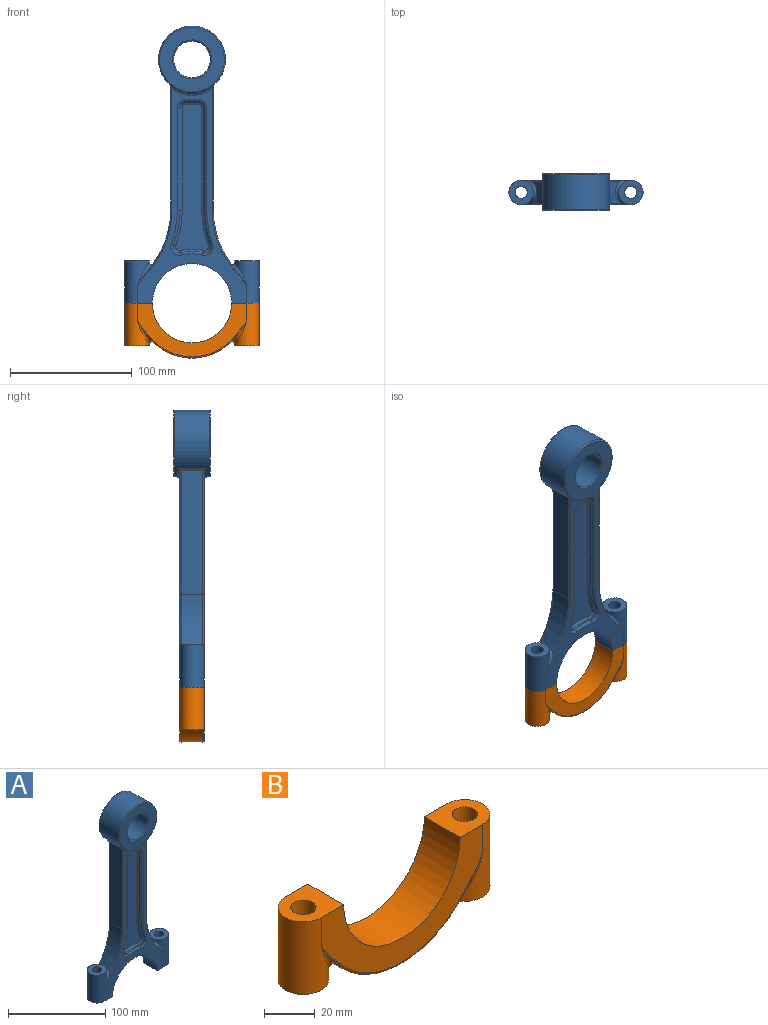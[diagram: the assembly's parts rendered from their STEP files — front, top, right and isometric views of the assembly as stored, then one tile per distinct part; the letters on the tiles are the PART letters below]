
ASSEMBLY  parts=2 mates=1
PART A: 119 faces, bbox 110.6x30.6x230.3 mm
  f0: plane 22.5x20mm, normal (0,0,-1), area 328.5mm2, adj f2,f9,f24,f29,f71
  f1: cylinder r=45mm len=0.99mm, axis (0,1,0), area 0.5mm2, adj f4,f50,f65
  f2: cylinder r=32.5mm len=65mm, axis (0,1,0), area 2042mm2, adj f0,f3,f9,f71
  f3: plane 22.5x20mm, normal (0,0,-1), area 328.5mm2, adj f2,f9,f26,f27,f71
  f4: cylinder r=75mm len=47.78mm, axis (0,1,0), area 891.8mm2, adj f1,f5,f50,f64,f69,f114
  f5: plane 101.42x19.35mm, normal (1,0,0), area 1826.5mm2, adj f4,f54,f62,f63,f112,f113
  f6: plane 101.42x19.35mm, normal (-1,0,0), area 1826.5mm2, adj f7,f52,f56,f57,f106,f107
  f7: cylinder r=75mm len=47.78mm, axis (0,1,0), area 891.8mm2, adj f6,f8,f51,f58,f70,f108
  f8: cylinder r=45mm len=0.99mm, axis (0,1,0), area 0.5mm2, adj f7,f51,f59
  f9: plane 176.13x90.58mm, normal (0,-1,0), area 2805.8mm2, adj f0,f2,f3,f24,f27,f30,f31,f32
  f10: cylinder r=15mm len=30mm, axis (0,1,0), area 2638.9mm2, adj f67,f117
  f11: cylinder r=27.5mm len=55mm, axis (0,1,0), area 3884.8mm2, adj f52,f53,f54,f68,f104,f118
  f12: plane 53x53mm, normal (0,-1,0), area 1401.9mm2, adj f67,f68
  f13: cylinder r=82.5mm len=28.36mm, axis (0,-1,0), area 57.9mm2, adj f14,f22,f33,f43
  f14: plane 83.87x2mm, normal (-1,0,0), area 167.7mm2, adj f13,f15,f35,f45
  f15: cylinder r=5mm len=5.63mm, axis (0,-1,0), area 17mm2, adj f14,f16,f37,f47
  f16: cylinder r=35mm len=8.75mm, axis (0,-1,0), area 17.5mm2, adj f15,f17,f39,f49
  f17: cylinder r=5mm len=5.63mm, axis (0,-1,0), area 17mm2, adj f16,f18,f38,f48
  f18: plane 83.87x2mm, normal (1,0,0), area 167.7mm2, adj f17,f19,f36,f46
  f19: cylinder r=82.5mm len=28.36mm, axis (0,-1,0), area 57.9mm2, adj f18,f20,f34,f44
  f20: cylinder r=5mm len=6.72mm, axis (0,-1,0), area 21.4mm2, adj f19,f21,f32,f42
  f21: cylinder r=42.5mm len=18.49mm, axis (0,-1,0), area 37.3mm2, adj f20,f22,f30,f40
  f22: cylinder r=5mm len=6.72mm, axis (0,-1,0), area 21.4mm2, adj f13,f21,f31,f41
  f23: plane 119.95x26.67mm, normal (0,-1,0), area 2035.7mm2, adj f40,f41,f42,f43,f44,f45,f46,f47
  f24: cylinder r=10mm len=35mm, axis (0,0,-1), area 1328.1mm2, adj f0,f9,f25,f51,f71
  f25: plane 20x20mm, normal (0,0,1), area 235.6mm2, adj f24,f29
  f26: cylinder r=5mm len=35mm, axis (0,0,-1), area 1099.6mm2, adj f3,f28
  f27: cylinder r=10mm len=35mm, axis (0,0,-1), area 1328.1mm2, adj f3,f9,f28,f50,f71
  f28: plane 20x20mm, normal (0,0,1), area 235.6mm2, adj f26,f27
  f29: cylinder r=5mm len=35mm, axis (0,0,-1), area 1099.6mm2, adj f0,f25
  f30: torus R=40.5mm, axis (0,-1,0), area 57.6mm2, adj f9,f21,f31,f32
  f31: torus R=7mm, axis (0,-1,0), area 38.5mm2, adj f9,f22,f30,f33
  f32: torus R=7mm, axis (0,-1,0), area 38.5mm2, adj f9,f20,f30,f34
  f33: torus R=80.5mm, axis (0,-1,0), area 90.2mm2, adj f9,f13,f31,f35
  f34: torus R=80.5mm, axis (0,-1,0), area 90.2mm2, adj f9,f19,f32,f36
  f35: cylinder r=2mm len=83.87mm, axis (0,0,-1), area 263.5mm2, adj f9,f14,f33,f37
  f36: cylinder r=2mm len=83.87mm, axis (0,0,1), area 263.5mm2, adj f9,f18,f34,f38
  f37: torus R=7mm, axis (0,-1,0), area 30.5mm2, adj f9,f15,f35,f39
  f38: torus R=7mm, axis (0,-1,0), area 30.5mm2, adj f9,f17,f36,f39
  f39: torus R=33mm, axis (0,-1,0), area 27mm2, adj f9,f16,f37,f38
  f40: torus R=44.5mm, axis (0,-1,0), area 59.6mm2, adj f21,f23,f41,f42
  f41: torus R=3mm, axis (0,-1,0), area 28.7mm2, adj f22,f23,f40,f43
  f42: torus R=3mm, axis (0,-1,0), area 28.7mm2, adj f20,f23,f40,f44
  f43: torus R=84.5mm, axis (0,-1,0), area 91.8mm2, adj f13,f23,f41,f45
  f44: torus R=84.5mm, axis (0,-1,0), area 91.8mm2, adj f19,f23,f42,f46
  f45: cylinder r=2mm len=83.87mm, axis (0,0,1), area 263.5mm2, adj f14,f23,f43,f47
  f46: cylinder r=2mm len=83.87mm, axis (0,0,-1), area 263.5mm2, adj f18,f23,f44,f48
  f47: torus R=3mm, axis (0,-1,0), area 22.8mm2, adj f15,f23,f45,f49
  f48: torus R=3mm, axis (0,-1,0), area 22.8mm2, adj f17,f23,f46,f49
  f49: torus R=37mm, axis (0,-1,0), area 28.1mm2, adj f16,f23,f47,f48
  f50: bspline ~25.23x24mm, area 140.7mm2, adj f1,f4,f27,f66,f69,f116
  f51: bspline ~24x22.8mm, area 140.7mm2, adj f7,f8,f24,f60,f70,f110
  f52: cylinder r=2mm len=24mm, axis (0,1,0), area 36.8mm2, adj f6,f11,f55,f105
  f53: torus R=29.5mm, axis (0,-1,0), area 115.8mm2, adj f9,f11,f55,f56,f61,f62
  f54: cylinder r=2mm len=24mm, axis (0,1,0), area 36.8mm2, adj f5,f11,f61,f111
  f55: bspline ~2.63x2.41mm, area 1.1mm2, adj f52,f53,f56
  f56: bspline ~3.49x1.51mm, area 2.9mm2, adj f6,f53,f55,f57
  f57: cylinder r=1mm len=99.1mm, axis (0,0,1), area 155.7mm2, adj f6,f9,f56,f58
  f58: torus R=76mm, axis (0,-1,0), area 81.8mm2, adj f7,f9,f57,f59
  f59: torus R=44mm, axis (0,-1,0), area 2mm2, adj f8,f9,f58,f60
  f60: bspline ~14.55x10.63mm, area 7.6mm2, adj f9,f51,f59
  f61: bspline ~2.63x2.41mm, area 1.1mm2, adj f53,f54,f62
  f62: bspline ~3.49x1.51mm, area 2.9mm2, adj f5,f53,f61,f63
  f63: cylinder r=1mm len=99.1mm, axis (0,0,-1), area 155.7mm2, adj f5,f9,f62,f64
  f64: torus R=76mm, axis (0,-1,0), area 81.8mm2, adj f4,f9,f63,f65
  f65: torus R=44mm, axis (0,-1,0), area 2mm2, adj f1,f9,f64,f66
  f66: bspline ~14.55x10.63mm, area 7.6mm2, adj f9,f50,f65
  f67: torus R=16mm, axis (0,-1,0), area 151.6mm2, adj f10,f12
  f68: torus R=26.5mm, axis (0,-1,0), area 267.8mm2, adj f11,f12
  f69: cylinder r=45mm len=0.99mm, axis (0,-1,0), area 0.5mm2, adj f4,f50,f115
  f70: cylinder r=45mm len=0.99mm, axis (0,-1,0), area 0.5mm2, adj f7,f51,f109
  f71: plane 176.13x90.58mm, normal (0,1,0), area 2805.8mm2, adj f0,f2,f3,f24,f27,f84,f85,f86
  f72: plane 53x53mm, normal (0,1,0), area 1401.9mm2, adj f117,f118
  f73: cylinder r=82.5mm len=28.36mm, axis (0,1,0), area 57.9mm2, adj f74,f82,f87,f97
  f74: plane 83.87x2mm, normal (-1,0,0), area 167.7mm2, adj f73,f75,f89,f99
  f75: cylinder r=5mm len=5.63mm, axis (0,1,0), area 17mm2, adj f74,f76,f91,f101
  f76: cylinder r=35mm len=8.75mm, axis (0,1,0), area 17.5mm2, adj f75,f77,f93,f103
  f77: cylinder r=5mm len=5.63mm, axis (0,1,0), area 17mm2, adj f76,f78,f92,f102
  f78: plane 83.87x2mm, normal (1,0,0), area 167.7mm2, adj f77,f79,f90,f100
  f79: cylinder r=82.5mm len=28.36mm, axis (0,1,0), area 57.9mm2, adj f78,f80,f88,f98
  f80: cylinder r=5mm len=6.72mm, axis (0,1,0), area 21.4mm2, adj f79,f81,f86,f96
  f81: cylinder r=42.5mm len=18.49mm, axis (0,1,0), area 37.3mm2, adj f80,f82,f84,f94
  f82: cylinder r=5mm len=6.72mm, axis (0,1,0), area 21.4mm2, adj f73,f81,f85,f95
  f83: plane 119.95x26.67mm, normal (0,1,0), area 2035.7mm2, adj f94,f95,f96,f97,f98,f99,f100,f101
  f84: torus R=40.5mm, axis (0,1,0), area 57.6mm2, adj f71,f81,f85,f86
  f85: torus R=7mm, axis (0,1,0), area 38.5mm2, adj f71,f82,f84,f87
  f86: torus R=7mm, axis (0,1,0), area 38.5mm2, adj f71,f80,f84,f88
  f87: torus R=80.5mm, axis (0,1,0), area 90.2mm2, adj f71,f73,f85,f89
  f88: torus R=80.5mm, axis (0,1,0), area 90.2mm2, adj f71,f79,f86,f90
  f89: cylinder r=2mm len=83.87mm, axis (0,0,-1), area 263.5mm2, adj f71,f74,f87,f91
  f90: cylinder r=2mm len=83.87mm, axis (0,0,1), area 263.5mm2, adj f71,f78,f88,f92
  f91: torus R=7mm, axis (0,1,0), area 30.5mm2, adj f71,f75,f89,f93
  f92: torus R=7mm, axis (0,1,0), area 30.5mm2, adj f71,f77,f90,f93
  f93: torus R=33mm, axis (0,1,0), area 27mm2, adj f71,f76,f91,f92
  f94: torus R=44.5mm, axis (0,1,0), area 59.6mm2, adj f81,f83,f95,f96
  f95: torus R=3mm, axis (0,1,0), area 28.7mm2, adj f82,f83,f94,f97
  f96: torus R=3mm, axis (0,1,0), area 28.7mm2, adj f80,f83,f94,f98
  f97: torus R=84.5mm, axis (0,1,0), area 91.8mm2, adj f73,f83,f95,f99
  f98: torus R=84.5mm, axis (0,1,0), area 91.8mm2, adj f79,f83,f96,f100
  f99: cylinder r=2mm len=83.87mm, axis (0,0,1), area 263.5mm2, adj f74,f83,f97,f101
  f100: cylinder r=2mm len=83.87mm, axis (0,0,-1), area 263.5mm2, adj f78,f83,f98,f102
  f101: torus R=3mm, axis (0,1,0), area 22.8mm2, adj f75,f83,f99,f103
  f102: torus R=3mm, axis (0,1,0), area 22.8mm2, adj f77,f83,f100,f103
  f103: torus R=37mm, axis (0,1,0), area 28.1mm2, adj f76,f83,f101,f102
  f104: torus R=29.5mm, axis (0,1,0), area 115.8mm2, adj f11,f71,f105,f106,f111,f112
  f105: bspline ~2.63x2.41mm, area 1.1mm2, adj f52,f104,f106
  f106: bspline ~3.49x1.51mm, area 2.9mm2, adj f6,f104,f105,f107
  f107: cylinder r=1mm len=99.1mm, axis (0,0,1), area 155.7mm2, adj f6,f71,f106,f108
  f108: torus R=76mm, axis (0,1,0), area 81.8mm2, adj f7,f71,f107,f109
  f109: torus R=44mm, axis (0,1,0), area 2mm2, adj f70,f71,f108,f110
  f110: bspline ~14.55x10.63mm, area 7.6mm2, adj f51,f71,f109
  f111: bspline ~2.63x2.41mm, area 1.1mm2, adj f54,f104,f112
  f112: bspline ~3.49x1.51mm, area 2.9mm2, adj f5,f104,f111,f113
  f113: cylinder r=1mm len=99.1mm, axis (0,0,-1), area 155.7mm2, adj f5,f71,f112,f114
  f114: torus R=76mm, axis (0,1,0), area 81.8mm2, adj f4,f71,f113,f115
  f115: torus R=44mm, axis (0,1,0), area 2mm2, adj f69,f71,f114,f116
  f116: bspline ~14.55x10.63mm, area 7.6mm2, adj f50,f71,f115
  f117: torus R=16mm, axis (0,1,0), area 151.6mm2, adj f10,f72
  f118: torus R=26.5mm, axis (0,1,0), area 267.8mm2, adj f11,f72
PART B: 20 faces, bbox 110.6x24.6x49.3 mm
  f0: plane 22.5x20mm, normal (0,0,1), area 328.5mm2, adj f2,f4,f8,f9,f16
  f1: cylinder r=45mm len=70.97mm, axis (0,1,0), area 1323.7mm2, adj f11,f12,f14,f18
  f2: cylinder r=32.5mm len=65mm, axis (0,1,0), area 2042mm2, adj f0,f3,f4,f16
  f3: plane 22.5x20mm, normal (0,0,1), area 328.5mm2, adj f2,f4,f5,f6,f16
  f4: plane 90.58x44.58mm, normal (0,-1,0), area 1472mm2, adj f0,f2,f3,f6,f9,f13,f14,f15
  f5: cylinder r=5mm len=35mm, axis (0,0,1), area 1099.6mm2, adj f3,f7
  f6: cylinder r=10mm len=35mm, axis (0,0,1), area 1328.1mm2, adj f3,f4,f7,f12,f16
  f7: plane 20x20mm, normal (0,0,-1), area 235.6mm2, adj f5,f6
  f8: cylinder r=5mm len=35mm, axis (0,0,1), area 1099.6mm2, adj f0,f10
  f9: cylinder r=10mm len=35mm, axis (0,0,1), area 1328.1mm2, adj f0,f4,f10,f11,f16
  f10: plane 20x20mm, normal (0,0,-1), area 235.6mm2, adj f8,f9
  f11: bspline ~25.23x24mm, area 152.7mm2, adj f1,f9,f15,f19
  f12: bspline ~24x22.8mm, area 152.7mm2, adj f1,f6,f13,f17
  f13: bspline ~14.55x10.63mm, area 7.6mm2, adj f4,f12,f14
  f14: torus R=44mm, axis (0,-1,0), area 127.4mm2, adj f1,f4,f13,f15
  f15: bspline ~14.55x10.63mm, area 7.6mm2, adj f4,f11,f14
  f16: plane 90.58x44.58mm, normal (0,1,0), area 1472mm2, adj f0,f2,f3,f6,f9,f17,f18,f19
  f17: bspline ~14.55x10.63mm, area 7.6mm2, adj f12,f16,f18
  f18: torus R=44mm, axis (0,1,0), area 127.4mm2, adj f1,f16,f17,f19
  f19: bspline ~14.55x10.63mm, area 7.6mm2, adj f11,f16,f18
PLACE A t=(-9.54,29.23,52.11)mm
PLACE B t=(-9.54,29.23,52.11)mm
MATE fastened B.f2 <-> A.f2  axis (0,1,0) through (-9.54,29.23,52.11)mm
